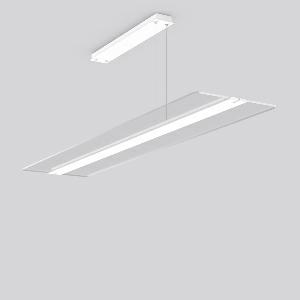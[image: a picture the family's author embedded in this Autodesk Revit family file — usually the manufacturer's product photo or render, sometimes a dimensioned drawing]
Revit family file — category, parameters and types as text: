
# Revit family: twindot_s_312265_002_1_76_8fb3
name_source: partatom
category: Lighting Fixtures
units: mm (PartAtom-declared; Revit-internal decimal feet)

## family parameters
Cut with Voids When Loaded = No
Host = Face
Light Source = No
Part Type = Normal
Room Calculation Point = No
Round Connector Dimension = Use Diameter
Shared = No

## types (1)
- TWINDOT S (1 x LED Modul 840, 8100 lm, 4000)
    Apparent Load = 62 VA
    CIE Flux Codes = 47 77 94 55 100
    Color Rendering = 80
    Color Temperature = 4000
    Default Elevation = 1800 mm
    Description = Series: TWINDOT S
LED pendant luminaire with extremely flat and frameless appearance. Middle bar made of aluminium extrusion profile, powder-coated. Transparent light guide made of UV-resistant acrylic glass (PMMA) with TWINDOT prismatic. Light control with perfectly glare-free TWINDOT technology for pleasantly gentle light with soft shadows. Even and wide indirect and direct light distribution. Direct 55%, indirect 45% light emission. 4-point steel cable suspension, steplessly adjustable. Converter integrated in the canopy (powder-coated white). Power supply through suspension cable. 
Colour: traffic white, matt (RAL 9016)
Length: 1500 mm
Width: 350 mm
Height: 20 mm
Suspension length: 500-1200 mm
Lamp: LED
Socket: without socket
Colour temperature: 4000K
Colour rendering index (CRI): 80
System power: 62 W
Rated luminous flux: 8100 lm
Luminous efficiency: 131 lm/W
Control gear: Converter, dimmable, DALI
Protection class: I
Type of protection: IP 20
    Height = 20 mm  [stored 0.0656168 ft]
    Lamp = 1 x LED Modul 840
    Lamp Light Flux = 8100 lm
    Lamp count = 1
    Length = 1500 mm
    Lifetime = 50000 h
    Luminous efficacy = 131 lm/W
    Manufacturer = RZB
    ModVariant = No
    Model = 312265.002.1.76
    Mounting Place = Ceiling
    Mounting Type = Pendant
    Number of Poles = 1
    OnlyDefault = Yes
    Power Factor = 1
    Product Name = TWINDOT S
    Product group = Pendant modular luminaires
    ProductGroupID = 906
    Protection Class = Protection class I
    Protection Degree = IP 20
    RLX_Detail_Level = 1
    RLX_Emergency_Light_Flux = 0 lm
    RLX_Emergency_Type = 0
    RLX_Emergency_Type_DB = No
    RlxData = <blob elided: 36565 chars, md5=b17bf1d3>
    Socket = socket
    Standby Power = 0 W
    System Light Flux = 8100 lm
    System Power = 62 W
    Type Comments = Product without accessories
    Type Image = 312265.002.jpg
    URL = http://relux.com
    VarID = ---
    Voltage = 230 V
    Voltage Range = 220-240 V
    Weight = 0.00 kg
    Width = 350 mm

note: [stored X ft] marks values corroborated as IEEE doubles in the binary element streams (Revit-internal decimal feet)

## geometry (parser evidence)
native form markers: Blend x4, Sweep x10
no freeform markers — native parametric forms only
